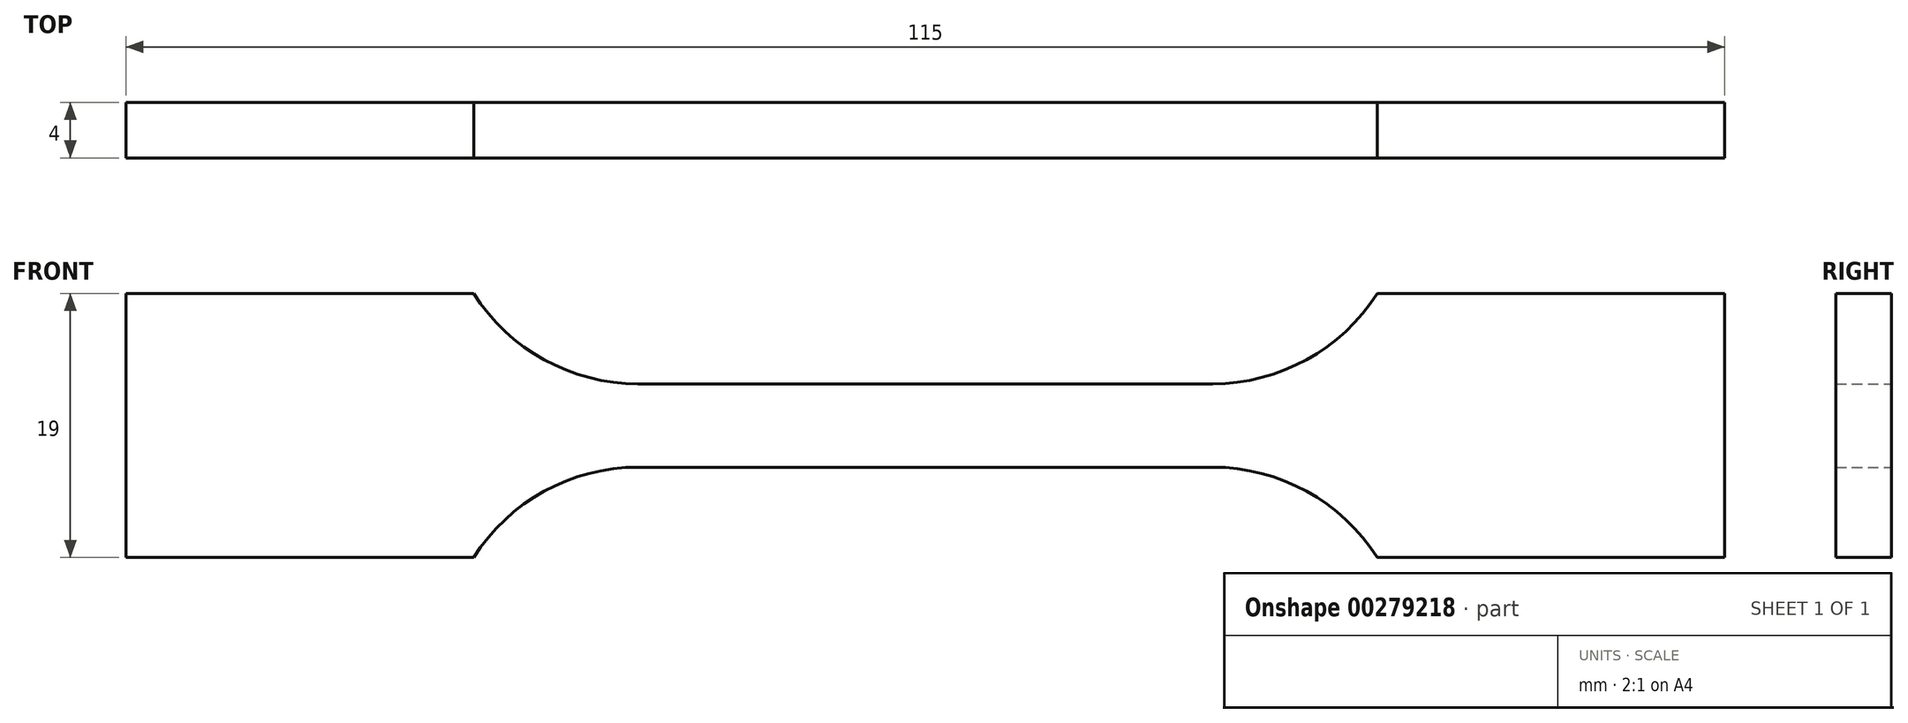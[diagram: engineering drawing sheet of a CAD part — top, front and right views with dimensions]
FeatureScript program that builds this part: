
annotation { "Feature Type Name" : "Feature", "Feature Type Description" : "" }
export const myFeature = defineFeature(function(context is Context, id is Id, definition is map)
    precondition{}
    {
        {
            var Q0;
            Q0=qCreatedBy(makeId("Front.planeOp"),FACE);
            var sketch = newSketch(context, id + "F0", { "sketchPlane" : qUnion([Q0])});
            skLineSegment(sketch, "E0", {"start": v(0, 3) * mm, "end": v(20.68, 3) * mm});
            skArc(sketch, "E1", {"start": v(20.68, 3) * mm, "mid": v(27.42, 4.73) * mm, "end": v(32.5, 9.5) * mm});
            skLineSegment(sketch, "E2", {"start": v(32.5, 9.5) * mm, "end": v(57.5, 9.5) * mm});
            skLineSegment(sketch, "E3.MirrorCS", {"start": v(0, -3) * mm, "end": v(20.68, -3) * mm});
            skLineSegment(sketch, "E4.MirrorCS", {"start": v(32.5, -9.5) * mm, "end": v(57.5, -9.5) * mm});
            skArc(sketch, "E5.MirrorCS", {"start": v(20.68, -3) * mm, "mid": v(27.42, -4.73) * mm, "end": v(32.5, -9.5) * mm});
            skArc(sketch, "E6.MirrorCS", {"start": v(-20.68, -3) * mm, "mid": v(-27.42, -4.73) * mm, "end": v(-32.5, -9.5) * mm});
            skArc(sketch, "E7.MirrorCS", {"start": v(-20.68, 3) * mm, "mid": v(-27.42, 4.73) * mm, "end": v(-32.5, 9.5) * mm});
            skLineSegment(sketch, "E8.MirrorCS", {"start": v(0, 3) * mm, "end": v(-20.68, 3) * mm});
            skLineSegment(sketch, "E9.MirrorCS", {"start": v(0, -3) * mm, "end": v(-20.68, -3) * mm});
            skLineSegment(sketch, "E10.MirrorCS", {"start": v(-32.5, 9.5) * mm, "end": v(-57.5, 9.5) * mm});
            skLineSegment(sketch, "E11.MirrorCS", {"start": v(-32.5, -9.5) * mm, "end": v(-57.5, -9.5) * mm});
            skLineSegment(sketch, "E12", {"start": v(-57.5, -9.5) * mm, "end": v(-57.5, 9.5) * mm});
            skLineSegment(sketch, "E13", {"start": v(57.5, 9.5) * mm, "end": v(57.5, -9.5) * mm});
            skSolve(sketch);
        }
        {
            var Q0;
            Q0 = qSketchRegion(id + "F0", true);
            extrude(context, id + "F1", {"entities" : qUnion([Q0]), "endBound" : BoundingType.SYMMETRIC, "depth" : 4 * mm});
        }
    });
